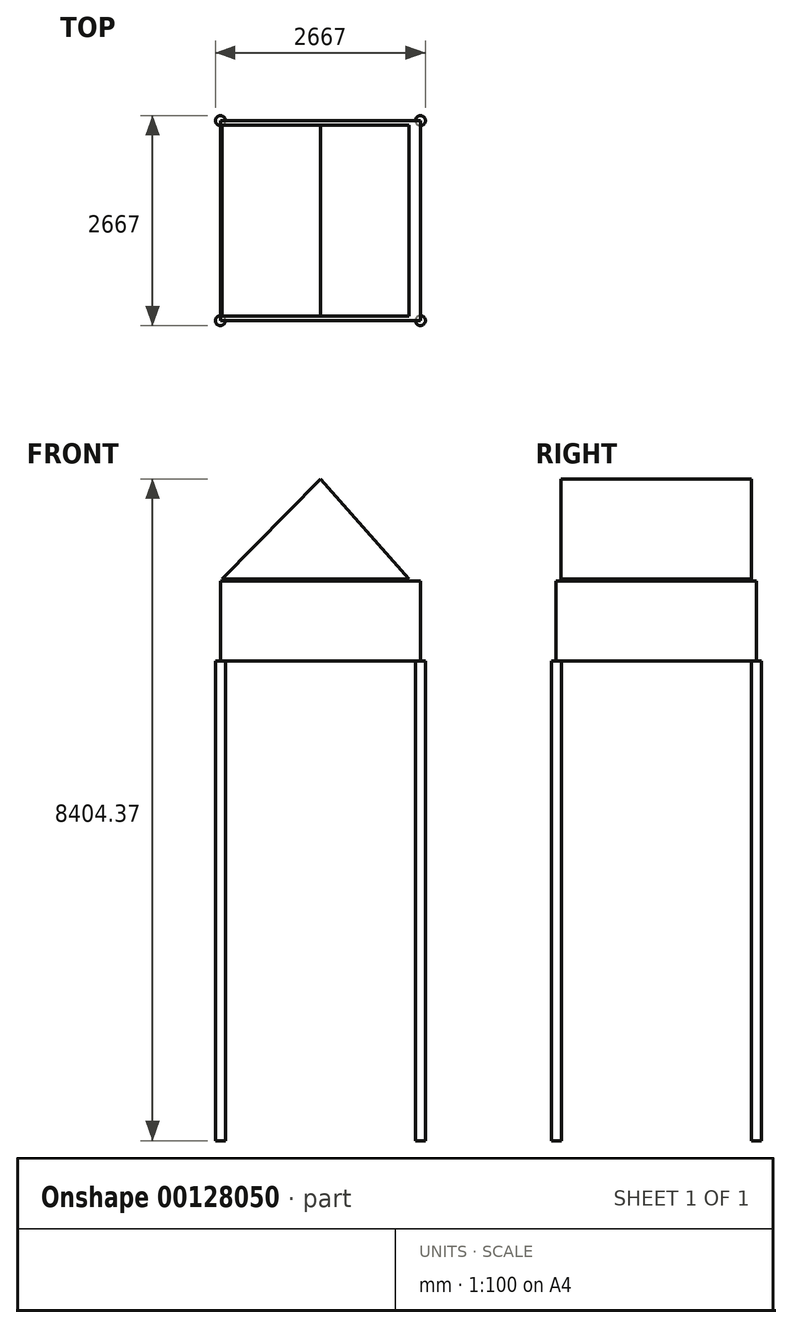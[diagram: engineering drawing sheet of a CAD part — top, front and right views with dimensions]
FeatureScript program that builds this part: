
annotation { "Feature Type Name" : "Feature", "Feature Type Description" : "" }
export const myFeature = defineFeature(function(context is Context, id is Id, definition is map)
    precondition{}
    {
        {
            var Q0;
            Q0=qCreatedBy(makeId("Top.planeOp"),FACE);
            var sketch = newSketch(context, id + "F0", { "sketchPlane" : qUnion([Q0])});
            skCircle(sketch, "E0", {"center": v(-1270, 1270) * mm, "radius": 63.5 * mm});
            skCircle(sketch, "E1.MirrorC", {"center": v(1270, 1270) * mm, "radius": 63.5 * mm});
            skCircle(sketch, "E2.MirrorC", {"center": v(-1270, -1270) * mm, "radius": 63.5 * mm});
            skCircle(sketch, "E3.MirrorC", {"center": v(1270, -1270) * mm, "radius": 63.5 * mm});
            skSolve(sketch);
        }
        {
            var Q0;
            Q0 = qSketchRegion(id + "F0", true);
            extrude(context, id + "F1", {"entities" : qUnion([Q0]), "depth" : 6096 * mm});
        }
        {
            var Q0;
            Q0=makeQuery(id+"F1.opExtrude","CAP_FACE",FACE,{"disambiguationData":[OSD([sQuery(id+"F0.wireOp",EDGE,"E0")])],"isStart":false});
            var sketch = newSketch(context, id + "F2", { "sketchPlane" : qUnion([Q0])});
            skLineSegment(sketch, "E4.bottom", {"start": v(-1270, 1270) * mm, "end": v(1272.92, 1270) * mm});
            skLineSegment(sketch, "E4.top", {"start": v(-1270, -1272.97) * mm, "end": v(1272.92, -1272.97) * mm});
            skLineSegment(sketch, "E4.left", {"start": v(-1270, 1270) * mm, "end": v(-1270, -1272.97) * mm});
            skLineSegment(sketch, "E4.right", {"start": v(1272.92, 1270) * mm, "end": v(1272.92, -1272.97) * mm});
            skSolve(sketch);
        }
        {
            var Q0;
            Q0 = qSketchRegion(id + "F2", true);
            extrude(context, id + "F3", {"entities" : qUnion([Q0]), "depth" : 1016 * mm});
        }
        {
            var Q0;
            Q0=qCreatedBy(makeId("Front.planeOp"),FACE);
            var sketch = newSketch(context, id + "F4", { "sketchPlane" : qUnion([Q0])});
            skLineSegment(sketch, "E5", {"start": v(1125.5, 7133.54) * mm, "end": v(-1246.53, 7133.54) * mm});
            skLineSegment(sketch, "E6", {"start": v(-1246.53, 7133.54) * mm, "end": v(0, 8404.37) * mm});
            skLineSegment(sketch, "E7", {"start": v(0, 8404.37) * mm, "end": v(1125.5, 7133.54) * mm});
            skSolve(sketch);
        }
        {
            var Q0;
            Q0 = qSketchRegion(id + "F4", true);
            extrude(context, id + "F5", {"entities" : qUnion([Q0]), "endBound" : BoundingType.SYMMETRIC, "depth" : 2422.7 * mm});
        }
        {
            var Q0;
            Q0=qCreatedBy(makeId("Front.planeOp"),FACE);
            cPlane(context, id + "F6", {"entities" : qUnion([Q0]), "cplaneType" : CPlaneType.OFFSET, "offset" : 1270 * mm, "width" : 152.4 * mm, "height" : 152.4 * mm});
        }
    });
